# Revit family: EKF_EE_Пластрон2УровняFORT(3шт)_PROxima
name_source: partatom
category: Электрооборудование
units: mm (PartAtom-declared; Revit-internal decimal feet)

## family parameters
Всегда вертикально = Нет
На основе рабочей плоскости = Да
Общий = Да
При загрузке вырезать с полостями = Нет
Размер круглого соединителя = Использовать диаметр
Тип детали = Силовой щит
Точка расчета площади = Нет

## types (4) — shared parameters
ADSK_Единица измерения = шт.
ADSK_Завод-изготовитель = EKF
ADSK_Количество = 1
ADSK_Марка = Пластрон FORT
ADSK_Материал = Сталь, с порошковым покрытием, белый
ADSK_Обозначение = Пластрон FORT
ADSK_Размер_Высота = 499 мм
ADSK_Размер_Глубина = 8 мм
Изготовитель = EKF
Серия номенклатуры = PROxima
Степень защиты IP = -
ТВ = EKF_2
Тип установки = -
Шаг = 700 мм
zero-valued in all types: ADSK_Масса, Отметка по умолчанию

## per-type parameters (varying)
| type | ADSK_Код изделия | ADSK_Размер_Ширина | Тип |
| Пластрон FORT высотой 500мм под 2 уровня мод. авт. выкл. для шкафа шириной 1000мм (3шт.) EKF PROxima | FMP50100 | 917 мм | 331 мм |
| Пластрон FORT высотой 500мм под 2 уровня мод. авт. выкл. для шкафа шириной 400мм (3шт.) EKF PROxima | FMP5040 | 317 мм | 332 мм |
| Пластрон FORT высотой 500мм под 2 уровня мод. авт. выкл. для шкафа шириной 600мм (3шт.) EKF PROxima | FMP5060 | 517 мм | 333 мм |
| Пластрон FORT высотой 500мм под 2 уровня мод. авт. выкл. для шкафа шириной 800мм (3шт.) EKF PROxima | FMP5080 | 717 мм | 334 мм |

note: column(s) folded — value = type name in every type: ADSK_Наименование
